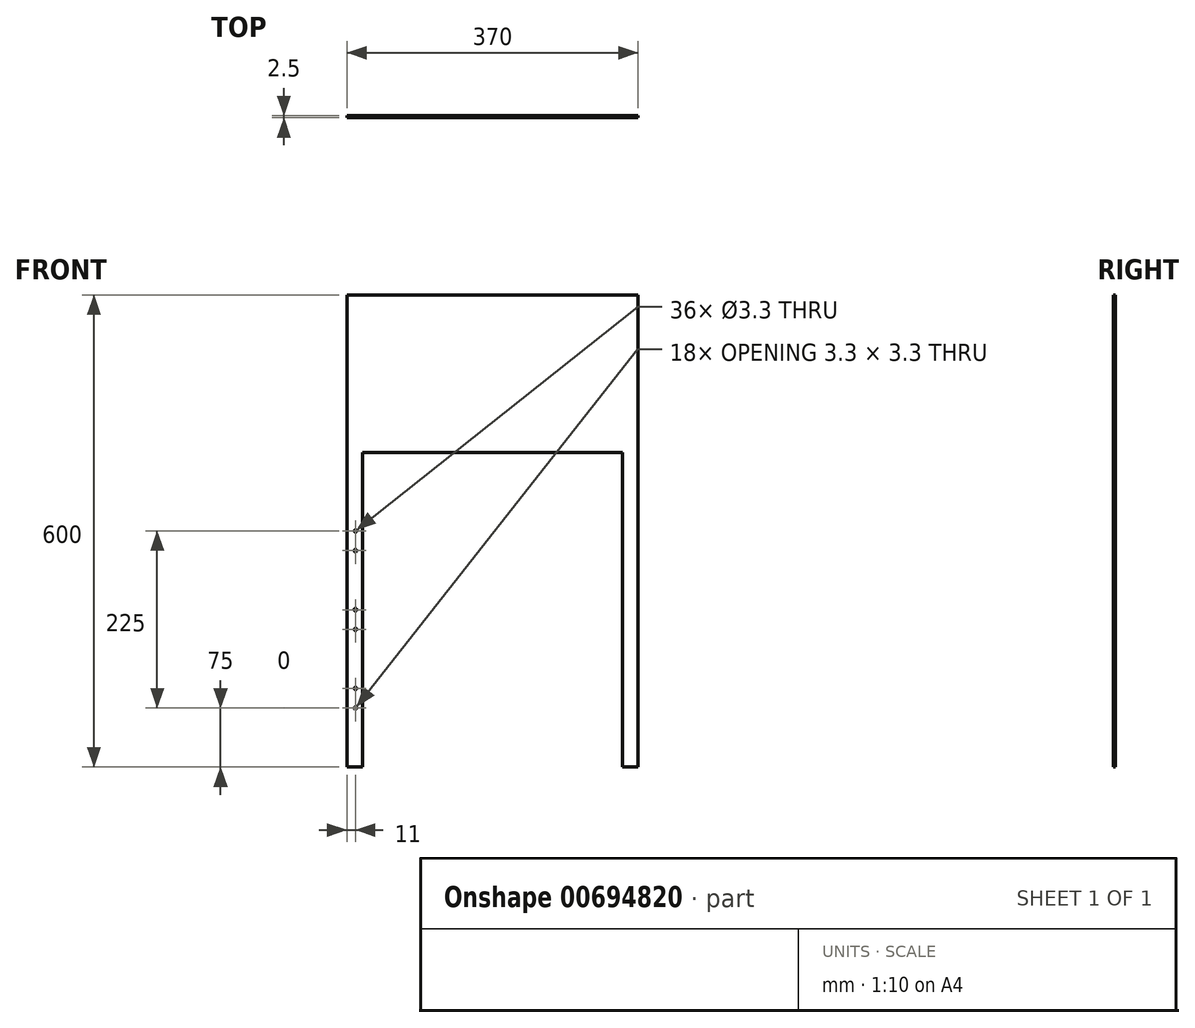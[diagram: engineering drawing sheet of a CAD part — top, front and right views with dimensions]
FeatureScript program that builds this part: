
annotation { "Feature Type Name" : "Feature", "Feature Type Description" : "" }
export const myFeature = defineFeature(function(context is Context, id is Id, definition is map)
    precondition{}
    {
        {
            var Q0;
            Q0=qCreatedBy(makeId("Front.planeOp"),FACE);
            var sketch = newSketch(context, id + "F0", { "sketchPlane" : qUnion([Q0])});
            skLineSegment(sketch, "E0.bottom", {"start": v(0, 0) * mm, "end": v(330, 0) * mm});
            skLineSegment(sketch, "E0.left", {"start": v(0, 0) * mm, "end": v(0, -400) * mm});
            skLineSegment(sketch, "E0.right", {"start": v(330, 0) * mm, "end": v(330, -400) * mm});
            skLineSegment(sketch, "E1.bottom", {"start": v(-20, 200) * mm, "end": v(350, 200) * mm});
            skLineSegment(sketch, "E1.left", {"start": v(-20, 200) * mm, "end": v(-20, -400) * mm});
            skLineSegment(sketch, "E1.right", {"start": v(350, 200) * mm, "end": v(350, -400) * mm});
            skLineSegment(sketch, "E2", {"start": v(-20, -400) * mm, "end": v(0, -400) * mm});
            skLineSegment(sketch, "E3", {"start": v(330, -400) * mm, "end": v(350, -400) * mm});
            skPoint(sketch, "E4", {"position": v(0, -300) * mm});
            skPoint(sketch, "E5", {"position": v(0, -200) * mm});
            skPoint(sketch, "E6", {"position": v(0, -100) * mm});
            skPoint(sketch, "E7", {"position": v(-9, -100) * mm});
            skPoint(sketch, "E8", {"position": v(-9, -200) * mm});
            skPoint(sketch, "E9", {"position": v(-9, -300) * mm});
            skPoint(sketch, "E10", {"position": v(-9, -125) * mm});
            skPoint(sketch, "E11", {"position": v(-9, -225) * mm});
            skPoint(sketch, "E12", {"position": v(-9, -325) * mm});
            skSolve(sketch);
        }
        {
            var Q0;
            Q0=qSketchRegion(id+"F0",true);
            extrude(context, id + "F1", {"entities" : qUnion([Q0]), "depth" : 2.5 * mm, "offsetDistance" : 25 * mm});
        }
        {
            var Q0;
            Q0=sQuery(id+"F0.wireOp",VERTEX,"E7");
            var Q1;
            Q1=sQuery(id+"F0.wireOp",VERTEX,"E8");
            var Q2;
            Q2=sQuery(id+"F0.wireOp",VERTEX,"E9");
            var Q3;
            Q3=sQuery(id+"F0.wireOp",VERTEX,"E10");
            var Q4;
            Q4=sQuery(id+"F0.wireOp",VERTEX,"E11");
            var Q5;
            Q5=sQuery(id+"F0.wireOp",VERTEX,"E12");
            var Q6;
            Q6=makeQuery(id+"F1.opExtrude","SWEPT_BODY",BODY,{"disambiguationData":[OSD([sQuery(id+"F0.wireOp",EDGE,"E0.bottom"),sQuery(id+"F0.wireOp",EDGE,"E0.left"),sQuery(id+"F0.wireOp",EDGE,"E0.right"),sQuery(id+"F0.wireOp",EDGE,"E1.bottom"),sQuery(id+"F0.wireOp",EDGE,"E1.left"),sQuery(id+"F0.wireOp",EDGE,"E1.right"),sQuery(id+"F0.wireOp",EDGE,"E2"),sQuery(id+"F0.wireOp",EDGE,"E3")])]});
            hole(context, id + "F2", {"style" : HoleStyle.SIMPLE, "endStyle" : HoleEndStyle.BLIND, "oppositeDirection" : true, "standardTappedOrClearance" : lookupTablePath({ "standard" : "ISO", "fit" : "Normal", "size" : "M3", "type" : "Clearance" }), "standardBlindInLast" : lookupTablePath({ "fit" : "Standard", "standard" : "ISO", "size" : "M3", "type" : "Clearance" }), "holeDiameter" : 3.3 * mm, "majorDiameter" : 5 * mm, "holeDepth" : 40 * mm, "isTappedThrough" : true, "tappedDepth" : 12 * mm, "tapClearance" : 3, "locations" : qUnion([Q0, Q1, Q2, Q3, Q4, Q5]), "scope" : qUnion([Q6])});
        }
    });
